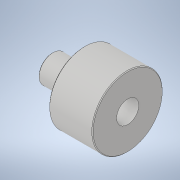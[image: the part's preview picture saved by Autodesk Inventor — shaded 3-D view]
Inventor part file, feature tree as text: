
AUTODESK INVENTOR PART (.ipt)
format: ipt  version: 2021 (Build 250183000, 183)  size: 120,832 bytes
history: native  units: in
note: dims shown in document units (in); Inventor stores cm internally (conversion verified against a paired STEP export)
features: extrude x2, sketch x2, chamfer x1
ambient origin geometry x8: Origin, YZ Plane, XZ Plane, XY Plane, X Axis, Y Axis, Z Axis, Center Point
bodies: Solid1 (feature_tree)
feature tree (5):
  extrude  "Extrusion1"  Depth=0.315in
  extrude  "Extrusion2"  Depth=0.5in
  chamfer  "Chamfer1"  Distance=0.616in
  sketch  "Sketch1"  dims[d0=0.394in d1=0.315in]
  sketch  "Sketch2"  dims[d2=0.453in d3=0.0in d4=1.0in d5=0.616in d6=0.0in d7=0.315in d9=0.01in d10=0.125in d11=45.0deg d12=0.5in d13=0.0344in d14=0.5in d15=0.0344in]
